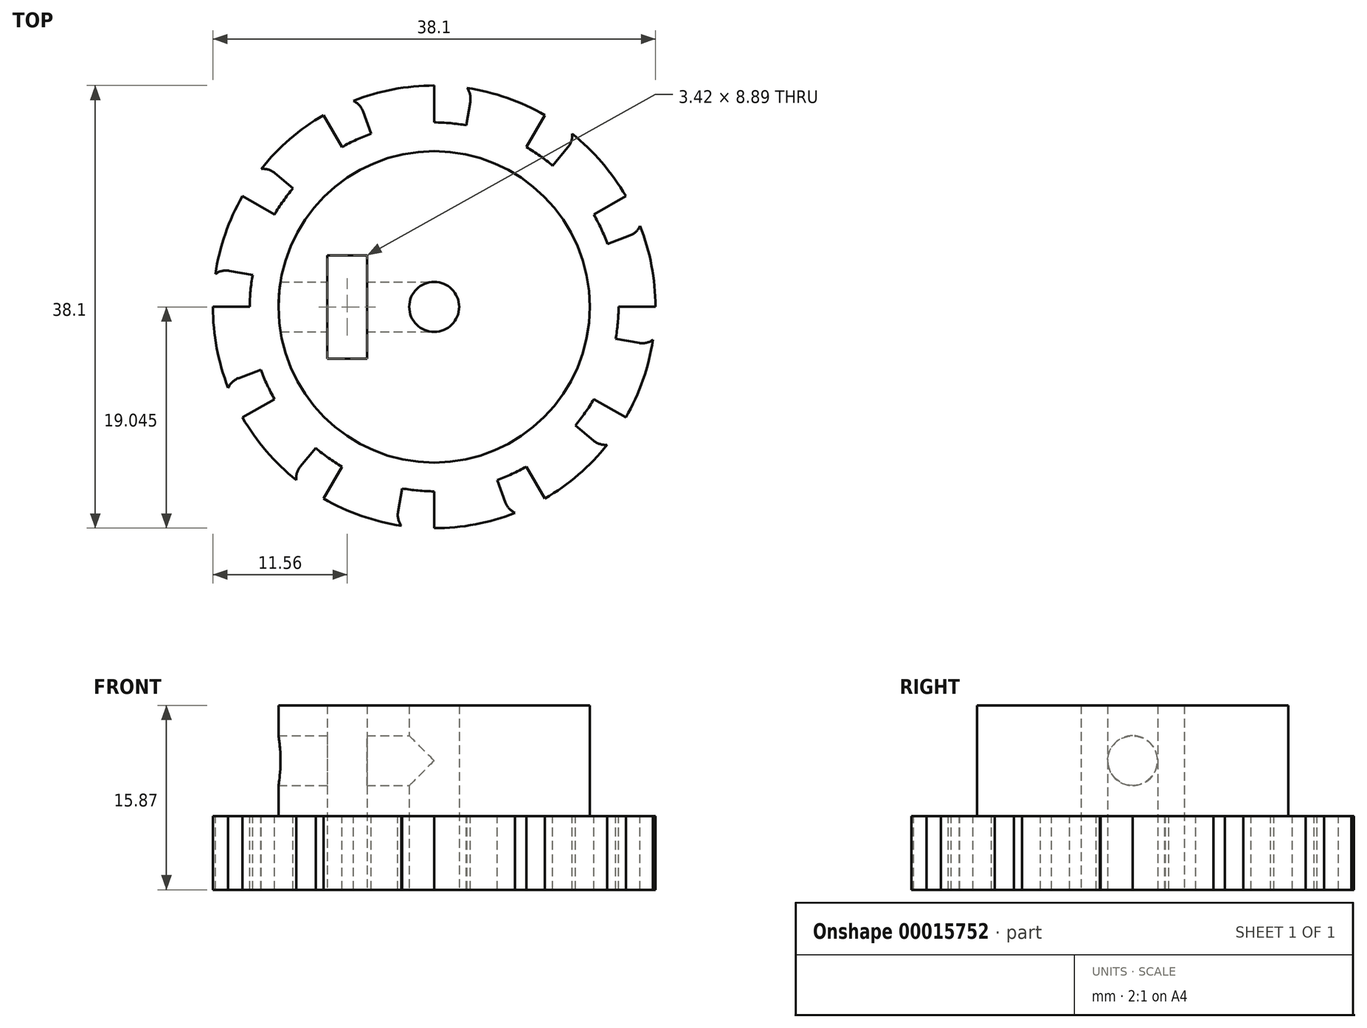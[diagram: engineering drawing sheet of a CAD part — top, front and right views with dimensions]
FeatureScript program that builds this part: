
annotation { "Feature Type Name" : "Feature", "Feature Type Description" : "" }
export const myFeature = defineFeature(function(context is Context, id is Id, definition is map)
    precondition{}
    {
        {
            var Q0;
            Q0=qCreatedBy(makeId("Top.planeOp"),FACE);
            var sketch = newSketch(context, id + "F0", { "sketchPlane" : qUnion([Q0])});
            skCircle(sketch, "E0", {"center": v(0, 0) * mm, "radius": 19.05 * mm});
            skCircle(sketch, "E1", {"center": v(0, 0) * mm, "radius": 2.15 * mm});
            skSolve(sketch);
        }
        {
            var Q0;
            Q0 = qSketchRegion(id + "F0", true);
            extrude(context, id + "F1", {"entities" : qUnion([Q0]), "depth" : 6.35 * mm});
        }
        {
            var Q0;
            Q0=makeQuery(id+"F1.opExtrude","CAP_FACE",FACE,{"disambiguationData":[OSD([sQuery(id+"F0.wireOp",EDGE,"E0"),sQuery(id+"F0.wireOp",EDGE,"E1")])],"isStart":false});
            var sketch = newSketch(context, id + "F2", { "sketchPlane" : qUnion([Q0])});
            skLineSegment(sketch, "E2", {"start": v(0, 0) * mm, "end": v(-15.88, 0) * mm, "construction": true});
            skLineSegment(sketch, "E3", {"start": v(0, 0) * mm, "end": v(-15.63, 2.76) * mm, "construction": true});
            skLineSegment(sketch, "E4", {"start": v(-15.63, 2.76) * mm, "end": v(-18.76, 3.3) * mm});
            skLineSegment(sketch, "E5", {"start": v(-15.88, 0) * mm, "end": v(-19.05, 0) * mm});
            skArc(sketch, "E6", {"start": v(-18.76, 3.3) * mm, "mid": v(-18.98, 1.66) * mm, "end": v(-19.05, 0) * mm});
            skArc(sketch, "E7", {"start": v(-15.63, 2.76) * mm, "mid": v(-15.81, 1.38) * mm, "end": v(-15.88, 0) * mm});
            skSolve(sketch);
        }
        {
            var Q0;
            Q0 = qSketchRegion(id + "F2", true);
            var Q1;
            Q1=makeQuery(id+"F1.opExtrude","CAP_FACE",FACE,{"disambiguationData":[OSD([sQuery(id+"F0.wireOp",EDGE,"E0"),sQuery(id+"F0.wireOp",EDGE,"E1")])],"isStart":true});
            extrude(context, id + "F3", {"entities" : qUnion([Q0]), "operationType" : NewBodyOperationType.REMOVE, "endBound" : BoundingType.UP_TO_SURFACE, "oppositeDirection" : true, "endBoundEntityFace" : qUnion([Q1]), "depth" : 25.4 * mm});
        }
        {
            var Q0;
            Q0=makeQuery(id+"F3.boolean.opBoolean","COPY",EDGE,{"derivedFrom":makeQuery(id+"F3.opExtrude","SWEPT_EDGE",EDGE,{"disambiguationData":[OSD([sQuery(id+"F0.wireOp",EDGE,"E0"),sQuery(id+"F2.wireOp",EDGE,"E4"),sQuery(id+"F2.wireOp",EDGE,"E6")])]})});
            var Q1;
            Q1=makeQuery(id+"F5.1.F3.boolean.opBoolean","COPY",EDGE,{"derivedFrom":makeQuery(id+"F5.1.F3.opExtrude","SWEPT_EDGE",EDGE,{"disambiguationData":[OSD([sQuery(id+"F0.wireOp",EDGE,"E0"),sQuery(id+"F2.wireOp",EDGE,"E5"),sQuery(id+"F2.wireOp",EDGE,"E6")])]})});
            var Q2;
            Q2=makeQuery(id+"F3.boolean.opBoolean","COPY",EDGE,{"derivedFrom":makeQuery(id+"F3.opExtrude","SWEPT_EDGE",EDGE,{"disambiguationData":[OSD([sQuery(id+"F0.wireOp",EDGE,"E0"),sQuery(id+"F2.wireOp",EDGE,"E5"),sQuery(id+"F2.wireOp",EDGE,"E6")])]})});
            fillet(context, id + "F4", {"entities" : qUnion([Q0, Q1, Q2]), "radius" : 1.59 * mm, "tangentPropagation" : true, "allowEdgeOverflow" : false});
        }
        {
            var Q0;
            Q0=makeQuery(id+"F3.boolean.opBoolean","COPY",FACE,{"derivedFrom":makeQuery(id+"F3.opExtrude","SWEPT_FACE",FACE,{"disambiguationData":[OSD([sQuery(id+"F2.wireOp",EDGE,"E7")])]})});
            var Q1;
            Q1=makeQuery(id+"F3.boolean.opBoolean","COPY",FACE,{"derivedFrom":makeQuery(id+"F3.opExtrude","SWEPT_FACE",FACE,{"disambiguationData":[OSD([sQuery(id+"F2.wireOp",EDGE,"E4")])]})});
            var Q2;
            Q2=makeQuery(id+"F4.opFillet","BLEND_FACE",FACE,{"disambiguationData":[OSD([sQuery(id+"F0.wireOp",EDGE,"E0"),sQuery(id+"F2.wireOp",EDGE,"E4"),sQuery(id+"F2.wireOp",EDGE,"E6")])]});
            var Q3;
            Q3=makeQuery(id+"F3.boolean.opBoolean","COPY",FACE,{"derivedFrom":makeQuery(id+"F3.opExtrude","SWEPT_FACE",FACE,{"disambiguationData":[OSD([sQuery(id+"F2.wireOp",EDGE,"E5")])]})});
            var Q4;
            Q4=makeQuery(id+"F4.opFillet","BLEND_FACE",FACE,{"disambiguationData":[OSD([sQuery(id+"F0.wireOp",EDGE,"E0"),sQuery(id+"F2.wireOp",EDGE,"E5"),sQuery(id+"F2.wireOp",EDGE,"E6")])]});
            var Q5;
            Q5=makeQuery(id+"F1.opExtrude","SWEPT_FACE",FACE,{"disambiguationData":[OSD([sQuery(id+"F0.wireOp",EDGE,"E0")])]});
            circularPattern(context, id + "F5", {"patternType" : PatternType.FACE, "faces" : qUnion([Q0, Q1, Q2, Q3, Q4]), "axis" : qUnion([Q5]), "angle" : 30 * degree, "instanceCount" : 12});
        }
        {
            var Q0;
            Q0=makeQuery(id+"F1.opExtrude","CAP_FACE",FACE,{"disambiguationData":[OSD([sQuery(id+"F0.wireOp",EDGE,"E0"),sQuery(id+"F0.wireOp",EDGE,"E1")])],"isStart":false});
            var sketch = newSketch(context, id + "F6", { "sketchPlane" : qUnion([Q0])});
            skLineSegment(sketch, "E8.bottom", {"start": v(-5.78, -4.45) * mm, "end": v(-9.2, -4.45) * mm});
            skLineSegment(sketch, "E8.top", {"start": v(-5.78, 4.44) * mm, "end": v(-9.2, 4.44) * mm});
            skLineSegment(sketch, "E8.left", {"start": v(-5.78, -4.45) * mm, "end": v(-5.78, 4.45) * mm});
            skLineSegment(sketch, "E8.right", {"start": v(-9.2, -4.45) * mm, "end": v(-9.2, 4.44) * mm});
            skLineSegment(sketch, "E9", {"start": v(0, 0) * mm, "end": v(-2.15, 0) * mm, "construction": true});
            skLineSegment(sketch, "E10", {"start": v(-2.15, 0) * mm, "end": v(-5.78, 0) * mm, "construction": true});
            skCircle(sketch, "E11", {"center": v(-9.2, 4.44) * mm, "radius": 3.18 * mm, "construction": true});
            skCircle(sketch, "E12", {"center": v(0, 0) * mm, "radius": 13.4 * mm});
            skCircle(sketch, "E13", {"center": v(0, 0) * mm, "radius": 2.15 * mm});
            skCircle(sketch, "E14", {"center": v(0, 0) * mm, "radius": 5.78 * mm, "construction": true});
            skSolve(sketch);
        }
        {
            var Q0;
            Q0 = qSketchRegion(id + "F6", true);
            extrude(context, id + "F7", {"entities" : qUnion([Q0]), "operationType" : NewBodyOperationType.ADD, "depth" : 9.52 * mm});
        }
        {
            var Q0;
            Q0=makeQuery(id+"F7.boolean.opBoolean","SPLIT",FACE,{"disambiguationData":[TD([makeQuery(id+"F7.opExtrude","SWEPT_FACE",FACE,{"disambiguationData":[OSD([sQuery(id+"F6.wireOp",EDGE,"E8.bottom")])]})])],"derivedFrom":makeQuery(id+"F1.opExtrude","CAP_FACE",FACE,{"disambiguationData":[OSD([sQuery(id+"F0.wireOp",EDGE,"E0"),sQuery(id+"F0.wireOp",EDGE,"E1")])],"isStart":false})});
            var Q1;
            Q1=makeQuery(id+"F1.opExtrude","CAP_FACE",FACE,{"disambiguationData":[OSD([sQuery(id+"F0.wireOp",EDGE,"E0"),sQuery(id+"F0.wireOp",EDGE,"E1")])],"isStart":true});
            extrude(context, id + "F8", {"entities" : qUnion([Q0]), "operationType" : NewBodyOperationType.REMOVE, "endBound" : BoundingType.UP_TO_SURFACE, "oppositeDirection" : true, "endBoundEntityFace" : qUnion([Q1]), "depth" : 25.4 * mm});
        }
        {
            var Q0;
            {var subQ0=sQuery(id+"F6.wireOp",EDGE,"E8.right");Q0=makeQuery(id+"F8.boolean.opBoolean","MERGE",FACE,{"derivedFrom":[makeQuery(id+"F7.opExtrude","SWEPT_FACE",FACE,{"disambiguationData":[OSD([subQ0])]}),makeQuery(id+"F8.opExtrude","SWEPT_FACE",FACE,{"disambiguationData":[OSD([subQ0])]})]});}
            var sketch = newSketch(context, id + "F9", { "sketchPlane" : qUnion([Q0])});
            skLineSegment(sketch, "E15", {"start": v(0, 15.88) * mm, "end": v(0, 6.35) * mm, "construction": true});
            skCircle(sketch, "E16", {"center": v(0, 11.11) * mm, "radius": 2.15 * mm});
            skSolve(sketch);
        }
        {
            var Q0;
            Q0 = qSketchRegion(id + "F9", true);
            var Q1;
            Q1=makeQuery(id+"F7.opExtrude","SWEPT_FACE",FACE,{"disambiguationData":[OSD([sQuery(id+"F6.wireOp",EDGE,"E12")])]});
            var Q2;
            Q2=makeQuery(id+"F7.boolean.opBoolean","MERGE",FACE,{"derivedFrom":[makeQuery(id+"F1.opExtrude","SWEPT_FACE",FACE,{"disambiguationData":[OSD([sQuery(id+"F0.wireOp",EDGE,"E1")])]}),makeQuery(id+"F7.opExtrude","SWEPT_FACE",FACE,{"disambiguationData":[OSD([sQuery(id+"F6.wireOp",EDGE,"E13")])]})]});
            extrude(context, id + "F10", {"entities" : qUnion([Q0]), "operationType" : NewBodyOperationType.REMOVE, "endBound" : BoundingType.UP_TO_SURFACE, "oppositeDirection" : true, "endBoundEntityFace" : qUnion([Q1]), "depth" : 25.4 * mm, "hasSecondDirection" : true, "secondDirectionBound" : BoundingType.UP_TO_SURFACE, "secondDirectionOppositeDirection" : false, "secondDirectionBoundEntityFace" : qUnion([Q2]), "secondDirectionDepth" : 25.4 * mm});
        }
    });
